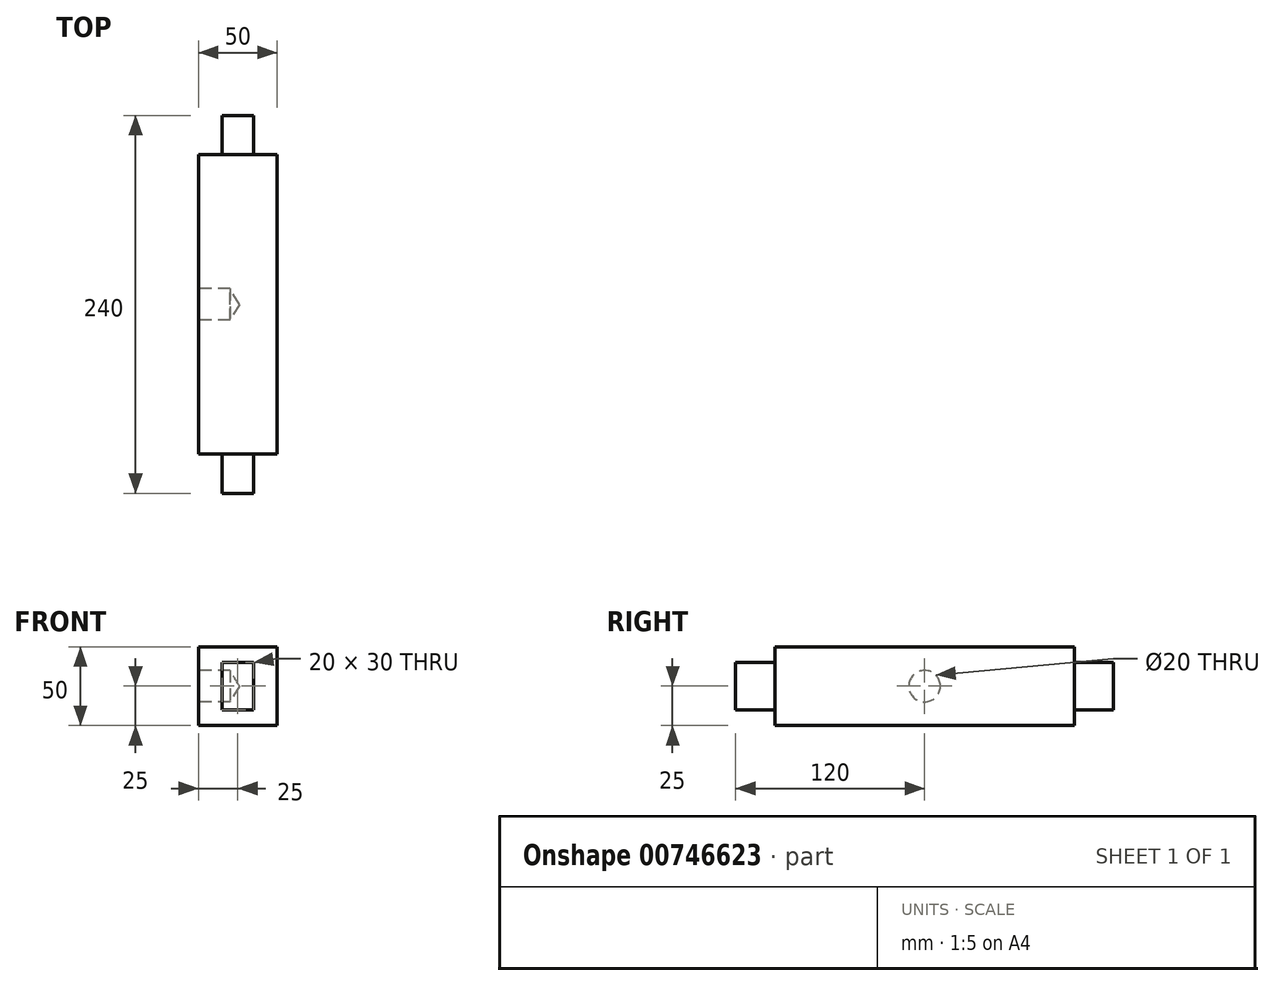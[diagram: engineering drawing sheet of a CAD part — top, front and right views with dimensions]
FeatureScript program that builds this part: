
annotation { "Feature Type Name" : "Feature", "Feature Type Description" : "" }
export const myFeature = defineFeature(function(context is Context, id is Id, definition is map)
    precondition{}
    {
        {
            var Q0;
            Q0=qCreatedBy(makeId("Front.planeOp"),FACE);
            var sketch = newSketch(context, id + "F0", { "sketchPlane" : qUnion([Q0])});
            skLineSegment(sketch, "E0.bottom", {"start": v(25, -25) * mm, "end": v(-25, -25) * mm});
            skLineSegment(sketch, "E0.top", {"start": v(25, 25) * mm, "end": v(-25, 25) * mm});
            skLineSegment(sketch, "E0.left", {"start": v(25, -25) * mm, "end": v(25, 25) * mm});
            skLineSegment(sketch, "E0.right", {"start": v(-25, -25) * mm, "end": v(-25, 25) * mm});
            skPoint(sketch, "E0.middle", {"position": v(0, 0) * mm});
            skLineSegment(sketch, "E1.bottom", {"start": v(10, -15) * mm, "end": v(-10, -15) * mm});
            skLineSegment(sketch, "E1.top", {"start": v(10, 15) * mm, "end": v(-10, 15) * mm});
            skLineSegment(sketch, "E1.left", {"start": v(10, -15) * mm, "end": v(10, 15) * mm});
            skLineSegment(sketch, "E1.right", {"start": v(-10, -15) * mm, "end": v(-10, 15) * mm});
            skSolve(sketch);
        }
        {
            var Q0;
            Q0=makeQuery(id+"F0.imprint","IMPRINT",FACE,{"disambiguationData":[TD([[makeQuery(id+"F0.imprint","IMPRINT",EDGE,{"derivedFrom":sQuery(id+"F0.wireOp",EDGE,"E0.bottom")}),-1.0]])]});
            var Q1;
            Q1=makeQuery(id+"F0.imprint","IMPRINT",FACE,{"disambiguationData":[TD([[makeQuery(id+"F0.imprint","IMPRINT",EDGE,{"derivedFrom":sQuery(id+"F0.wireOp",EDGE,"E1.bottom")}),-1.0]])]});
            extrude(context, id + "F1", {"entities" : qUnion([Q0, Q1]), "oppositeDirection" : true, "depth" : 240 * mm, "offsetDistance" : 25 * mm});
        }
        {
            var Q0;
            Q0=makeQuery(id+"F0.imprint","IMPRINT",FACE,{"disambiguationData":[TD([[makeQuery(id+"F0.imprint","IMPRINT",EDGE,{"derivedFrom":sQuery(id+"F0.wireOp",EDGE,"E0.bottom")}),-1.0]])]});
            extrude(context, id + "F2", {"entities" : qUnion([Q0]), "operationType" : NewBodyOperationType.REMOVE, "oppositeDirection" : true, "depth" : 25 * mm, "offsetDistance" : 25 * mm});
        }
        {
            var Q0;
            Q0=makeQuery(id+"F1.opExtrude","CAP_FACE",FACE,{"disambiguationData":[OSD([sQuery(id+"F0.wireOp",EDGE,"E0.bottom"),sQuery(id+"F0.wireOp",EDGE,"E0.top"),sQuery(id+"F0.wireOp",EDGE,"E0.left"),sQuery(id+"F0.wireOp",EDGE,"E0.right")])],"isStart":false});
            var sketch = newSketch(context, id + "F3", { "sketchPlane" : qUnion([Q0])});
            skLineSegment(sketch, "E2.bottom", {"start": v(10, -15) * mm, "end": v(-10, -15) * mm});
            skLineSegment(sketch, "E2.top", {"start": v(10, 15) * mm, "end": v(-10, 15) * mm});
            skLineSegment(sketch, "E2.left", {"start": v(10, -15) * mm, "end": v(10, 15) * mm});
            skLineSegment(sketch, "E2.right", {"start": v(-10, -15) * mm, "end": v(-10, 15) * mm});
            skPoint(sketch, "E2.middle", {"position": v(0, 0) * mm});
            skSolve(sketch);
        }
        {
            var Q0;
            Q0=makeQuery(id+"F3.imprint","IMPRINT",FACE,{"disambiguationData":[TD([[makeQuery(id+"F3.imprint","IMPRINT",EDGE,{"derivedFrom":sQuery(id+"F3.wireOp",EDGE,"E2.bottom")}),1.0]])]});
            extrude(context, id + "F4", {"entities" : qUnion([Q0]), "operationType" : NewBodyOperationType.REMOVE, "oppositeDirection" : true, "depth" : 25 * mm, "offsetDistance" : 25 * mm});
        }
        {
            var Q0;
            Q0=makeQuery(id+"F1.opExtrude","SWEPT_FACE",FACE,{"disambiguationData":[OSD([sQuery(id+"F0.wireOp",EDGE,"E0.right")])]});
            var sketch = newSketch(context, id + "F5", { "sketchPlane" : qUnion([Q0])});
            skPoint(sketch, "E3", {"position": v(-120, 0) * mm});
            skSolve(sketch);
        }
        {
            var Q0;
            Q0=sQuery(id+"F5.wireOp",VERTEX,"E3");
            var Q1;
            Q1=makeQuery(id+"F1.opExtrude","SWEPT_BODY",BODY,{"disambiguationData":[OSD([sQuery(id+"F0.wireOp",EDGE,"E0.bottom"),sQuery(id+"F0.wireOp",EDGE,"E0.top"),sQuery(id+"F0.wireOp",EDGE,"E0.left"),sQuery(id+"F0.wireOp",EDGE,"E0.right")])]});
            hole(context, id + "F6", {"style" : HoleStyle.SIMPLE, "endStyle" : HoleEndStyle.BLIND, "holeDiameter" : 20 * mm, "majorDiameter" : 5 * mm, "holeDepth" : 20 * mm, "isTappedThrough" : true, "tappedDepth" : 12 * mm, "tapClearance" : 3, "locations" : qUnion([Q0]), "scope" : qUnion([Q1])});
        }
    });
